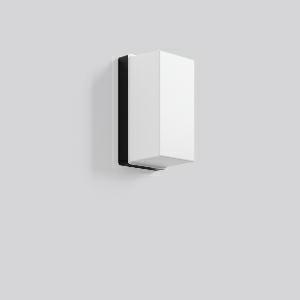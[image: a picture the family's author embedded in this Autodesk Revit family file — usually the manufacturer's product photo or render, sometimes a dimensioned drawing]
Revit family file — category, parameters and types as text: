
# Revit family: rechteck_22144_003_d56d
name_source: partatom
category: Lighting Fixtures
units: mm (PartAtom-declared; Revit-internal decimal feet)

## family parameters
Cut with Voids When Loaded = No
Host = Face
Light Source = No
Part Type = Normal
Room Calculation Point = No
Round Connector Dimension = Use Diameter
Shared = No

## types (1)
- RECHTECK (1 x QA60/clear E27, 700 lm, 46 W, 3000)
    Apparent Load = 46 VA
    CIE Flux Codes = 35 64 85 77 54
    Color Rendering = 90
    Color Temperature = 3000
    Default Elevation = 1800 mm
    Description = Series: RECHTECK
Rectangular surface-mounted luminaire in classic design. Base: plastic. Diffuser: plastic (polypropylene), opal, satin finish. Diffuser fastening: spring system. Suitable for Wall (surface). 
Colour: black
Length: 215 mm
Width: 115 mm
Height: 110 mm
Lamp: A60
Number of lamps: 1
Wattage: 60 W
Socket: E27
System power: 17 W
Rated luminous flux: 490 lm
Luminous efficiency: 29 lm/W
Control gear: Converter not necessary
Protection class: II
Type of protection: IP 44
    Height = 110 mm
    Lamp = 1 x QA60/clear E27
    Lamp Light Flux = 700 lm
    Lamp Power = 46 W
    Lamp count = 1
    Length = 215 mm
    Lifetime = 3000 h
    Luminous efficacy = 8 lm/W
    Manufacturer = RZB
    ModVariant = No
    Model = 22144.003
    Mounting Place = Wall, Ceiling
    Mounting Type = Surface mounted
    Number of Poles = 1
    OnlyDefault = Yes
    Power Factor = 1
    Product Name = RECHTECK
    Product group = Surface mounted ceiling and wall luminaires
    ProductGroupID = 305
    Protection Class = Protection class II
    Protection Degree = IP 44
    RLX_Detail_Level = 1
    RLX_Emergency_Light_Flux = 0 lm
    RLX_Emergency_Type = 0
    RLX_Emergency_Type_DB = No
    RlxData = <blob elided: 13365 chars, md5=787b975b>
    Socket = E27
    Standby Power = 0 W
    System Light Flux = 379 lm
    System Power = 46 W
    Type Comments = Product without accessories
    Type Image = 22144.003.jpg
    URL = http://relux.com
    VarID = ---
    Voltage = 230 V
    Voltage Range = 220-240 V
    Weight = 0.00 kg
    Width = 115 mm

## geometry (parser evidence)
native form markers: Sweep x10
no freeform markers — native parametric forms only
